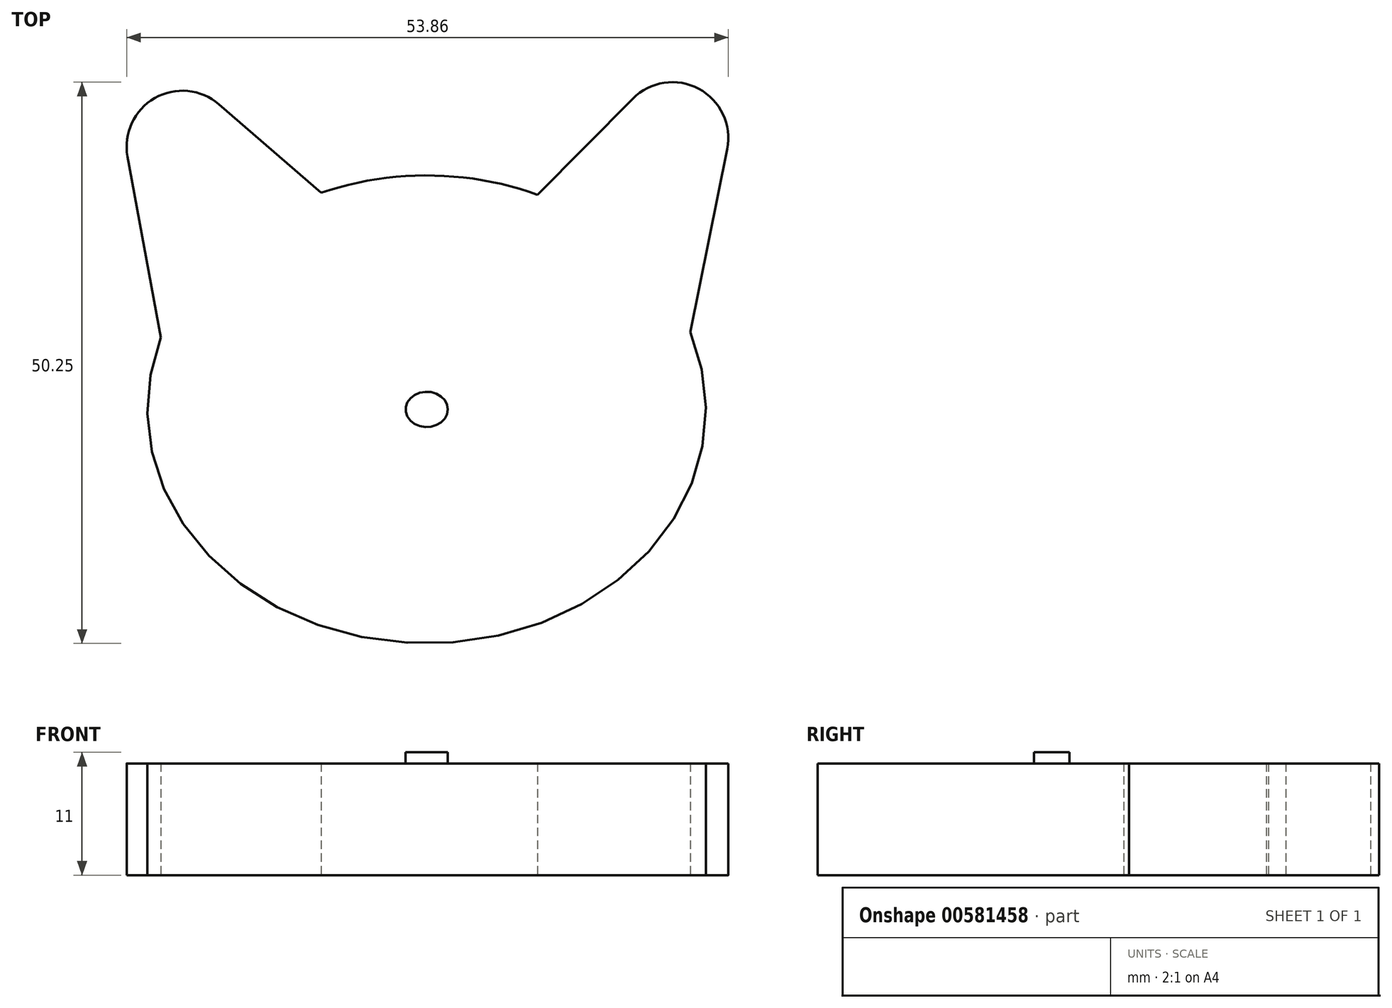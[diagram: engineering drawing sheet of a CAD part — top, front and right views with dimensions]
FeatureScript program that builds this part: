
annotation { "Feature Type Name" : "Feature", "Feature Type Description" : "" }
export const myFeature = defineFeature(function(context is Context, id is Id, definition is map)
    precondition{}
    {
        {
            var Q0;
            Q0=qCreatedBy(makeId("Top.planeOp"),FACE);
            var sketch = newSketch(context, id + "F0", { "sketchPlane" : qUnion([Q0])});
            skEllipse(sketch, "E0", {"center": v(0, 0) * mm, "majorRadius": 25 * mm, "minorRadius": 20.95 * mm, "majorAxis": v(1, 0)});
            skLineSegment(sketch, "E1", {"start": v(-9.44, 19.4) * mm, "end": v(-18.6, 27.32) * mm});
            skLineSegment(sketch, "E2", {"start": v(-26.78, 22.63) * mm, "end": v(-23.8, 6.44) * mm});
            skLineSegment(sketch, "E3", {"start": v(9.93, 19.23) * mm, "end": v(18.45, 27.82) * mm});
            skLineSegment(sketch, "E4", {"start": v(26.9, 23.31) * mm, "end": v(23.6, 6.93) * mm});
            skEllipse(sketch, "E5", {"center": v(0, 0) * mm, "majorRadius": 1.89 * mm, "minorRadius": 1.58 * mm, "majorAxis": v(1, 0)});
            skArc(sketch, "E6.filletArc", {"start": v(26.9, 23.31) * mm, "mid": v(24.35, 28.71) * mm, "end": v(18.45, 27.82) * mm});
            skArc(sketch, "E7.filletArc", {"start": v(-18.6, 27.32) * mm, "mid": v(-24.35, 27.88) * mm, "end": v(-26.78, 22.63) * mm});
            skSolve(sketch);
        }
        {
            var Q0;
            Q0=makeQuery(id+"F0.imprint","IMPRINT",FACE,{"disambiguationData":[TD([[makeQuery(id+"F0.imprint","IMPRINT",EDGE,{"derivedFrom":sQuery(id+"F0.wireOp",EDGE,"E5")}),-1.0]])]});
            var Q1;
            {var subQ0=sQuery(id+"F0.wireOp",EDGE,"E1");Q1=makeQuery(id+"F0.imprint","IMPRINT",FACE,{"disambiguationData":[TD([[makeQuery(id+"F0.imprint","IMPRINT",EDGE,{"derivedFrom":subQ0}),1.0]])]});}
            var Q2;
            {var subQ0=sQuery(id+"F0.wireOp",EDGE,"E3");Q2=makeQuery(id+"F0.imprint","IMPRINT",FACE,{"disambiguationData":[TD([[makeQuery(id+"F0.imprint","IMPRINT",EDGE,{"derivedFrom":subQ0}),-1.0]])]});}
            extrude(context, id + "F1", {"entities" : qUnion([Q0, Q1, Q2]), "depth" : 10 * mm, "offsetDistance" : 25.4 * mm});
        }
        {
            var Q0;
            Q0=makeQuery(id+"F0.imprint","IMPRINT",FACE,{"disambiguationData":[TD([[makeQuery(id+"F0.imprint","IMPRINT",EDGE,{"derivedFrom":sQuery(id+"F0.wireOp",EDGE,"E5")}),1.0]])]});
            extrude(context, id + "F2", {"entities" : qUnion([Q0]), "operationType" : NewBodyOperationType.ADD, "depth" : 11 * mm, "offsetDistance" : 25.4 * mm});
        }
    });
